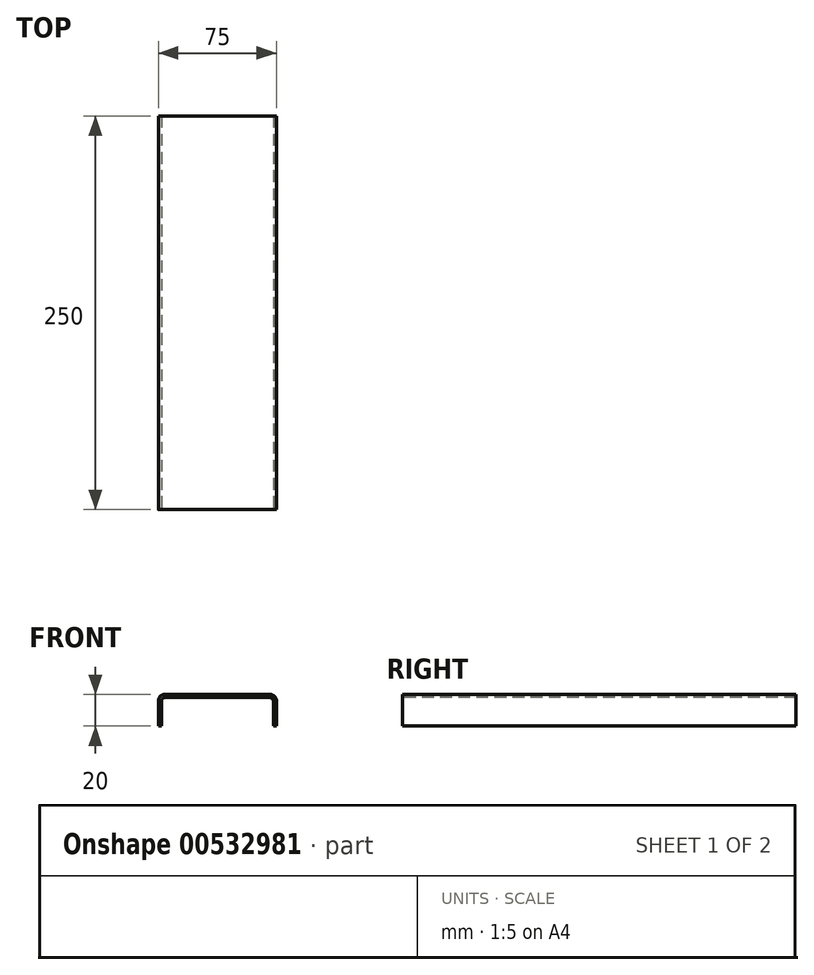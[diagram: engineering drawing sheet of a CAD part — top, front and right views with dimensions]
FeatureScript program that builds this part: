
annotation { "Feature Type Name" : "Feature", "Feature Type Description" : "" }
export const myFeature = defineFeature(function(context is Context, id is Id, definition is map)
    precondition{}
    {
        {
            var Q0;
            Q0=qCreatedBy(makeId("Front.planeOp"),FACE);
            var sketch = newSketch(context, id + "F0", { "sketchPlane" : qUnion([Q0])});
            skLineSegment(sketch, "E0", {"start": v(-144.45, 0) * mm, "end": v(-144.45, 16) * mm});
            skLineSegment(sketch, "E1", {"start": v(-140.45, 20) * mm, "end": v(-73.45, 20) * mm});
            skLineSegment(sketch, "E2", {"start": v(-69.45, 16) * mm, "end": v(-69.45, 0) * mm});
            skLineSegment(sketch, "E3.0", {"start": v(-142.45, 0) * mm, "end": v(-142.45, 16) * mm});
            skLineSegment(sketch, "E4.0", {"start": v(-140.45, 18) * mm, "end": v(-73.45, 18) * mm});
            skLineSegment(sketch, "E5.0", {"start": v(-71.45, 16) * mm, "end": v(-71.45, 0) * mm});
            skLineSegment(sketch, "E6", {"start": v(-69.45, 0) * mm, "end": v(-71.45, 0) * mm});
            skLineSegment(sketch, "E7", {"start": v(-142.45, 0) * mm, "end": v(-144.45, 0) * mm});
            skPoint(sketch, "E8.visualSharp", {"position": v(-142.45, 18) * mm});
            skArc(sketch, "E8.filletArc", {"start": v(-140.45, 18) * mm, "mid": v(-141.86, 17.41) * mm, "end": v(-142.45, 16) * mm});
            skPoint(sketch, "E9.visualSharp", {"position": v(-144.45, 20) * mm});
            skArc(sketch, "E9.filletArc", {"start": v(-140.45, 20) * mm, "mid": v(-143.28, 18.83) * mm, "end": v(-144.45, 16) * mm});
            skPoint(sketch, "E10.visualSharp", {"position": v(-71.45, 18) * mm});
            skArc(sketch, "E10.filletArc", {"start": v(-71.45, 16) * mm, "mid": v(-72.04, 17.41) * mm, "end": v(-73.45, 18) * mm});
            skPoint(sketch, "E11.visualSharp", {"position": v(-69.45, 20) * mm});
            skArc(sketch, "E11.filletArc", {"start": v(-69.45, 16) * mm, "mid": v(-70.62, 18.83) * mm, "end": v(-73.45, 20) * mm});
            skSolve(sketch);
        }
        {
            var Q0;
            Q0 = qSketchRegion(id + "F0", true);
            extrude(context, id + "F1", {"entities" : qUnion([Q0]), "oppositeDirection" : true, "depth" : 250 * mm, "offsetDistance" : 25 * mm});
        }
    });
